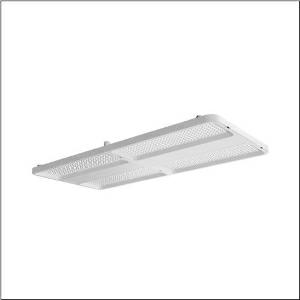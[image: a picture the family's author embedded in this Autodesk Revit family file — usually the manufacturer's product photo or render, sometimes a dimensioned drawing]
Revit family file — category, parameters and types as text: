
# Revit family: highbay_21_maxi_52hn12db4wda
name_source: partatom
category: Lighting Fixtures
units: mm (PartAtom-declared; Revit-internal decimal feet)

## family parameters
Cut with Voids When Loaded = No
Host = Face
Light Source = No
Part Type = Normal
Room Calculation Point = No
Round Connector Dimension = Use Diameter
Shared = No

## types (1)
- --- (1 x LED, 10140 lm, 55.2 W, 4000K)
    Apparent Load = 55 VA
    CIE Flux Codes = 90 98 100 100 100
    Color Rendering = 80
    Color Temperature = 4000K
    Default Elevation = 1800 mm
    Description = high bay luminaire Highbay 21 maxi; direct symmetric wide distribution, light control with lens of PMMA; UGR ≤ 22 (X = 4H | Y = 8H | S = 0.25H | reflection values 70/50/20); luminous flux: 64.000lm; light colour: 840, colour temperature: 4000K, MacAdam ≤ 3 SDCM (initial), colour rendering: CRI > 80; luminous efficacy: 185,5lm/W; rated service life: 75.000h (L80/B50) at AT= ta max; control: DALI 2; luminaire connection: terminal, 5-pole, max. 2.5mm² (cable entry for one cable, Ø 8.5..16mm); mains connection: 230..240V, AC/DC 0/50..60Hz; connected load: 345W; protection rating (complete): IP66; insulation class (complete): insulation class I (protective earthing); protection symbol: D; impact resistance: IK08; certification: CE, ENEC, VDE, UKCA; luminaire for central battery installations according to DIN EN 60598-2-22, internal wiring halogen-free; luminaire corresponds to IFS (International Featured Standards) requirements for safety and quality in the food industry; LABS conformity tested according to VDMA 24364:2018-05; housing frame of high-performance plastic PA6, matt traffic white (RAL 9016); cover of PMMA; dimension (LxWxH): 946 x 442 x 72mm; permissible operating ambient temperature: -40..+50°C (reducing of maximum allowable ambient temperature of 5°C with ceiling mounting); packaging unit: 1 piece; (delivery without accessories; please order mounting accessories separately)
    Height = 72 mm  [stored 0.23622 ft]
    Lamp = 1 x LED
    Lamp Light Flux = 10140 lm
    Lamp Power = 55.2 W
    Lamp count = 1
    Length = 946 mm
    Luminous efficacy = 184 lm/W
    Manufacturer = Siteco
    ModVariant = No
    Model = 52HN12DB4WDA
    Mounting Place = Ceiling
    Mounting Type = Pendant
    Number of Poles = 1
    OnlyDefault = Yes
    Power Factor = 1
    Product Name = Highbay 21 maxi
    Product group = high bay luminaire
    ProductGroupID = 901
    Protection Class = Protection class I
    Protection Degree = IP 66
    RLX_Detail_Level = 1
    RLX_Emergency_Light_Flux = 0 lm
    RLX_Emergency_Type = 0
    RLX_Emergency_Type_DB = No
    RlxData = <blob elided: 128177 chars, md5=05dcfca8>
    Socket = socket
    Standby Power = 0 W
    System Light Flux = 10140 lm
    System Power = 55 W
    Type Comments = : DC mode (central or group accumulator) initial emergency light level
    Type Image = l_1363244.jpg
    URL = http://relux.com
    VarID = @adj_016829
    Voltage = 0 V
    Weight = 0.00 kg
    Width = 442 mm

note: [stored X ft] marks values corroborated as IEEE doubles in the binary element streams (Revit-internal decimal feet)

## geometry (parser evidence)
native form markers: Blend x4, Sweep x9
no freeform markers — native parametric forms only
